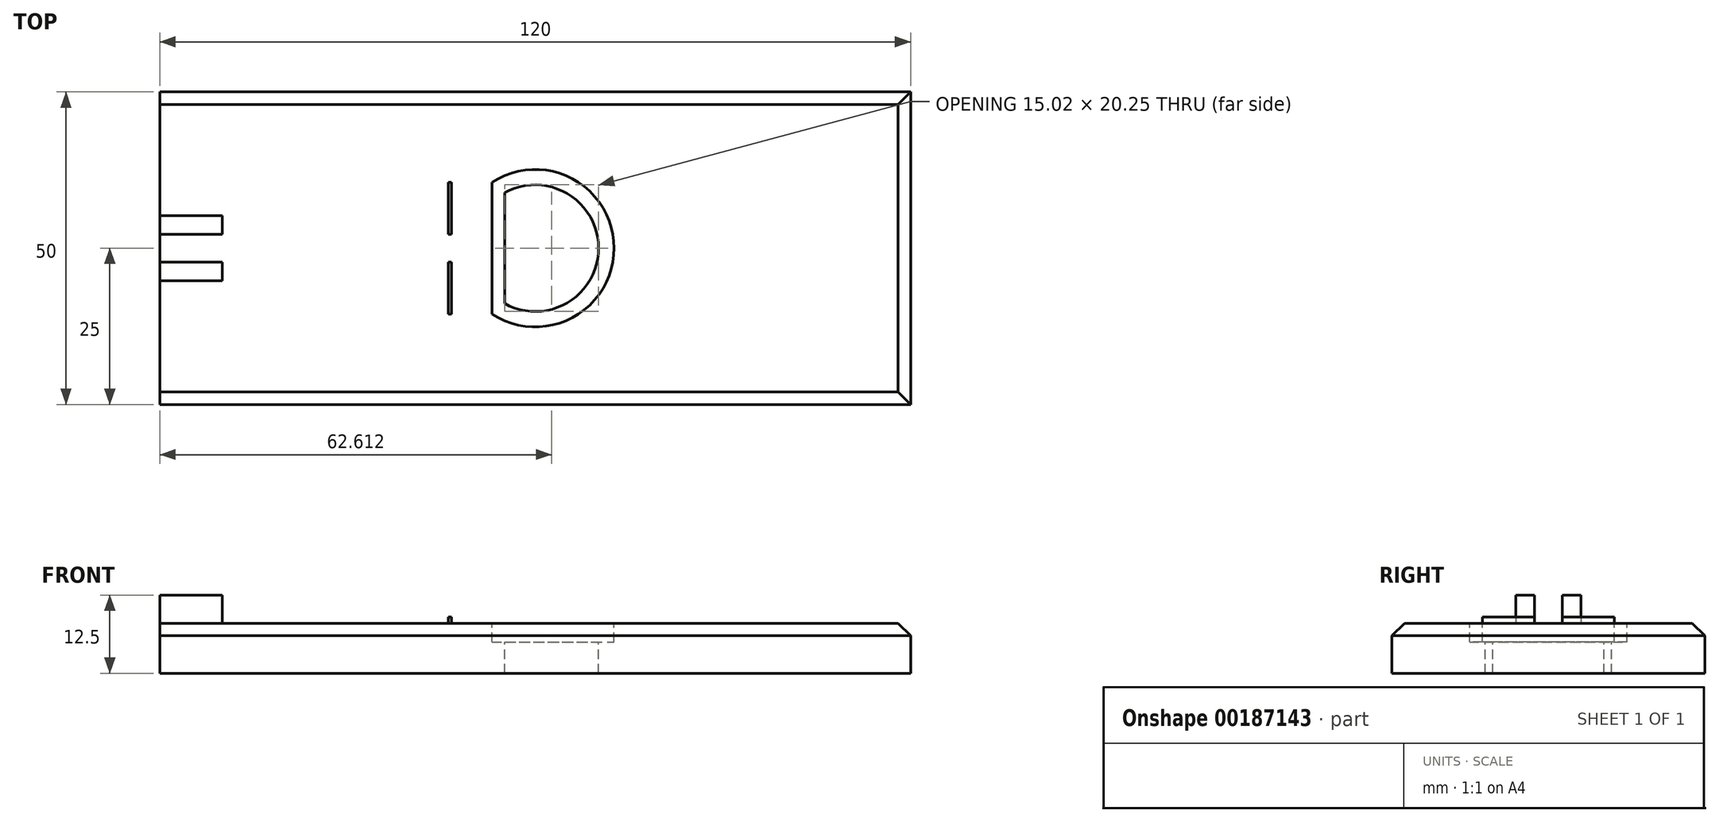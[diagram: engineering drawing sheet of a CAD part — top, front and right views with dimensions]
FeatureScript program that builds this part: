
annotation { "Feature Type Name" : "Feature", "Feature Type Description" : "" }
export const myFeature = defineFeature(function(context is Context, id is Id, definition is map)
    precondition{}
    {
        {
            var Q0;
            Q0=qCreatedBy(makeId("Top.planeOp"),FACE);
            var sketch = newSketch(context, id + "F0", { "sketchPlane" : qUnion([Q0])});
            skLineSegment(sketch, "E0.bottom", {"start": v(0, 0) * mm, "end": v(120, 0) * mm});
            skLineSegment(sketch, "E0.top", {"start": v(0, -50) * mm, "end": v(120, -50) * mm});
            skLineSegment(sketch, "E0.left", {"start": v(0, 0) * mm, "end": v(0, -50) * mm});
            skLineSegment(sketch, "E0.right", {"start": v(120, 0) * mm, "end": v(120, -50) * mm});
            skSolve(sketch);
        }
        {
            var Q0;
            Q0=makeQuery(id+"F0.imprint","IMPRINT",FACE,{"disambiguationData":[TD([[makeQuery(id+"F0.imprint","IMPRINT",EDGE,{"derivedFrom":sQuery(id+"F0.wireOp",EDGE,"E0.bottom")}),-1.0]])]});
            extrude(context, id + "F1", {"entities" : qUnion([Q0]), "depth" : 8 * mm});
        }
        {
            var Q0;
            Q0=makeQuery(id+"F1.opExtrude","CAP_FACE",FACE,{"disambiguationData":[OSD([sQuery(id+"F0.wireOp",EDGE,"E0.bottom"),sQuery(id+"F0.wireOp",EDGE,"E0.top"),sQuery(id+"F0.wireOp",EDGE,"E0.left"),sQuery(id+"F0.wireOp",EDGE,"E0.right")])],"isStart":false});
            var sketch = newSketch(context, id + "F2", { "sketchPlane" : qUnion([Q0])});
            skArc(sketch, "E1", {"start": v(53.1, -35.54) * mm, "mid": v(72.6, -25) * mm, "end": v(53.1, -14.46) * mm});
            skLineSegment(sketch, "E2", {"start": v(53.1, -14.46) * mm, "end": v(53.1, -35.54) * mm});
            skSolve(sketch);
        }
        {
            var Q0;
            Q0 = qSketchRegion(id + "F2", true);
            extrude(context, id + "F3", {"entities" : qUnion([Q0]), "operationType" : NewBodyOperationType.REMOVE, "oppositeDirection" : true, "depth" : (3) * mm});
        }
        {
            var Q0;
            Q0=makeQuery(id+"F3.boolean.opBoolean","COPY",FACE,{"derivedFrom":makeQuery(id+"F3.opExtrude","CAP_FACE",FACE,{"disambiguationData":[OSD([sQuery(id+"F2.wireOp",EDGE,"E1"),sQuery(id+"F2.wireOp",EDGE,"E2")])],"isStart":false})});
            var sketch = newSketch(context, id + "F4", { "sketchPlane" : qUnion([Q0])});
            skArc(sketch, "E3", {"start": v(55.1, -33.86) * mm, "mid": v(70.12, -25) * mm, "end": v(55.1, -16.14) * mm});
            skLineSegment(sketch, "E4", {"start": v(55.1, -16.14) * mm, "end": v(55.1, -33.86) * mm});
            skSolve(sketch);
        }
        {
            var Q0;
            Q0=makeQuery(id+"F4.imprint","IMPRINT",FACE,{"disambiguationData":[TD([[makeQuery(id+"F4.imprint","IMPRINT",EDGE,{"derivedFrom":sQuery(id+"F4.wireOp",EDGE,"E3")}),1.0]])]});
            extrude(context, id + "F5", {"entities" : qUnion([Q0]), "operationType" : NewBodyOperationType.REMOVE, "oppositeDirection" : true, "depth" : 25 * mm});
        }
        {
            var Q0;
            Q0=makeQuery(id+"F1.opExtrude","CAP_FACE",FACE,{"disambiguationData":[OSD([sQuery(id+"F0.wireOp",EDGE,"E0.bottom"),sQuery(id+"F0.wireOp",EDGE,"E0.top"),sQuery(id+"F0.wireOp",EDGE,"E0.left"),sQuery(id+"F0.wireOp",EDGE,"E0.right")])],"isStart":false});
            var sketch = newSketch(context, id + "F6", { "sketchPlane" : qUnion([Q0])});
            skLineSegment(sketch, "E5.bottom", {"start": v(0, -19.8) * mm, "end": v(10, -19.8) * mm});
            skLineSegment(sketch, "E5.top", {"start": v(0, -22.8) * mm, "end": v(10, -22.8) * mm});
            skLineSegment(sketch, "E5.left", {"start": v(0, -19.8) * mm, "end": v(0, -22.8) * mm});
            skLineSegment(sketch, "E6.bottom", {"start": v(0, -27.2) * mm, "end": v(10, -27.2) * mm});
            skLineSegment(sketch, "E6.top", {"start": v(0, -30.2) * mm, "end": v(10, -30.2) * mm});
            skLineSegment(sketch, "E6.left", {"start": v(0, -27.2) * mm, "end": v(0, -30.2) * mm});
            skLineSegment(sketch, "E7", {"start": v(10, -19.8) * mm, "end": v(10, -22.8) * mm});
            skLineSegment(sketch, "E8", {"start": v(10, -27.2) * mm, "end": v(10, -30.2) * mm});
            skSolve(sketch);
        }
        {
            var Q0;
            Q0 = qSketchRegion(id + "F6", true);
            extrude(context, id + "F7", {"entities" : qUnion([Q0]), "operationType" : NewBodyOperationType.ADD, "depth" : 4.5 * mm});
        }
        {
            var Q0;
            Q0=makeQuery(id+"F1.opExtrude","CAP_EDGE",EDGE,{"disambiguationData":[OSD([sQuery(id+"F0.wireOp",EDGE,"E0.right")])],"isStart":false});
            var Q1;
            Q1=makeQuery(id+"F1.opExtrude","CAP_EDGE",EDGE,{"disambiguationData":[OSD([sQuery(id+"F0.wireOp",EDGE,"E0.bottom")])],"isStart":false});
            var Q2;
            Q2=makeQuery(id+"F1.opExtrude","CAP_EDGE",EDGE,{"disambiguationData":[OSD([sQuery(id+"F0.wireOp",EDGE,"E0.top")])],"isStart":false});
            chamfer(context, id + "F8", {"entities" : qUnion([Q0, Q1, Q2]), "width" : 2 * mm, "tangentPropagation" : true});
        }
        {
            var Q0;
            Q0=makeQuery(id+"F1.opExtrude","CAP_FACE",FACE,{"disambiguationData":[OSD([sQuery(id+"F0.wireOp",EDGE,"E0.bottom"),sQuery(id+"F0.wireOp",EDGE,"E0.top"),sQuery(id+"F0.wireOp",EDGE,"E0.left"),sQuery(id+"F0.wireOp",EDGE,"E0.right")])],"isStart":false});
            var sketch = newSketch(context, id + "F9", { "sketchPlane" : qUnion([Q0])});
            skLineSegment(sketch, "E9.bottom", {"start": v(46.1, -14.46) * mm, "end": v(46.6, -14.46) * mm});
            skLineSegment(sketch, "E9.top", {"start": v(46.1, -22.8) * mm, "end": v(46.6, -22.8) * mm});
            skLineSegment(sketch, "E9.left", {"start": v(46.1, -14.46) * mm, "end": v(46.1, -22.8) * mm});
            skLineSegment(sketch, "E9.right", {"start": v(46.6, -14.46) * mm, "end": v(46.6, -22.8) * mm});
            skLineSegment(sketch, "E10.bottom", {"start": v(46.1, -27.2) * mm, "end": v(46.6, -27.2) * mm});
            skLineSegment(sketch, "E10.top", {"start": v(46.1, -35.54) * mm, "end": v(46.6, -35.54) * mm});
            skLineSegment(sketch, "E10.left", {"start": v(46.1, -27.2) * mm, "end": v(46.1, -35.54) * mm});
            skLineSegment(sketch, "E10.right", {"start": v(46.6, -27.2) * mm, "end": v(46.6, -35.54) * mm});
            skSolve(sketch);
        }
        {
            var Q0;
            Q0=makeQuery(id+"F9.imprint","IMPRINT",FACE,{"disambiguationData":[TD([[makeQuery(id+"F9.imprint","IMPRINT",EDGE,{"derivedFrom":sQuery(id+"F9.wireOp",EDGE,"E9.bottom")}),-1.0]])]});
            var Q1;
            Q1=makeQuery(id+"F9.imprint","IMPRINT",FACE,{"disambiguationData":[TD([[makeQuery(id+"F9.imprint","IMPRINT",EDGE,{"derivedFrom":sQuery(id+"F9.wireOp",EDGE,"E10.bottom")}),-1.0]])]});
            extrude(context, id + "F10", {"entities" : qUnion([Q0, Q1]), "operationType" : NewBodyOperationType.ADD, "depth" : 1 * mm});
        }
    });
